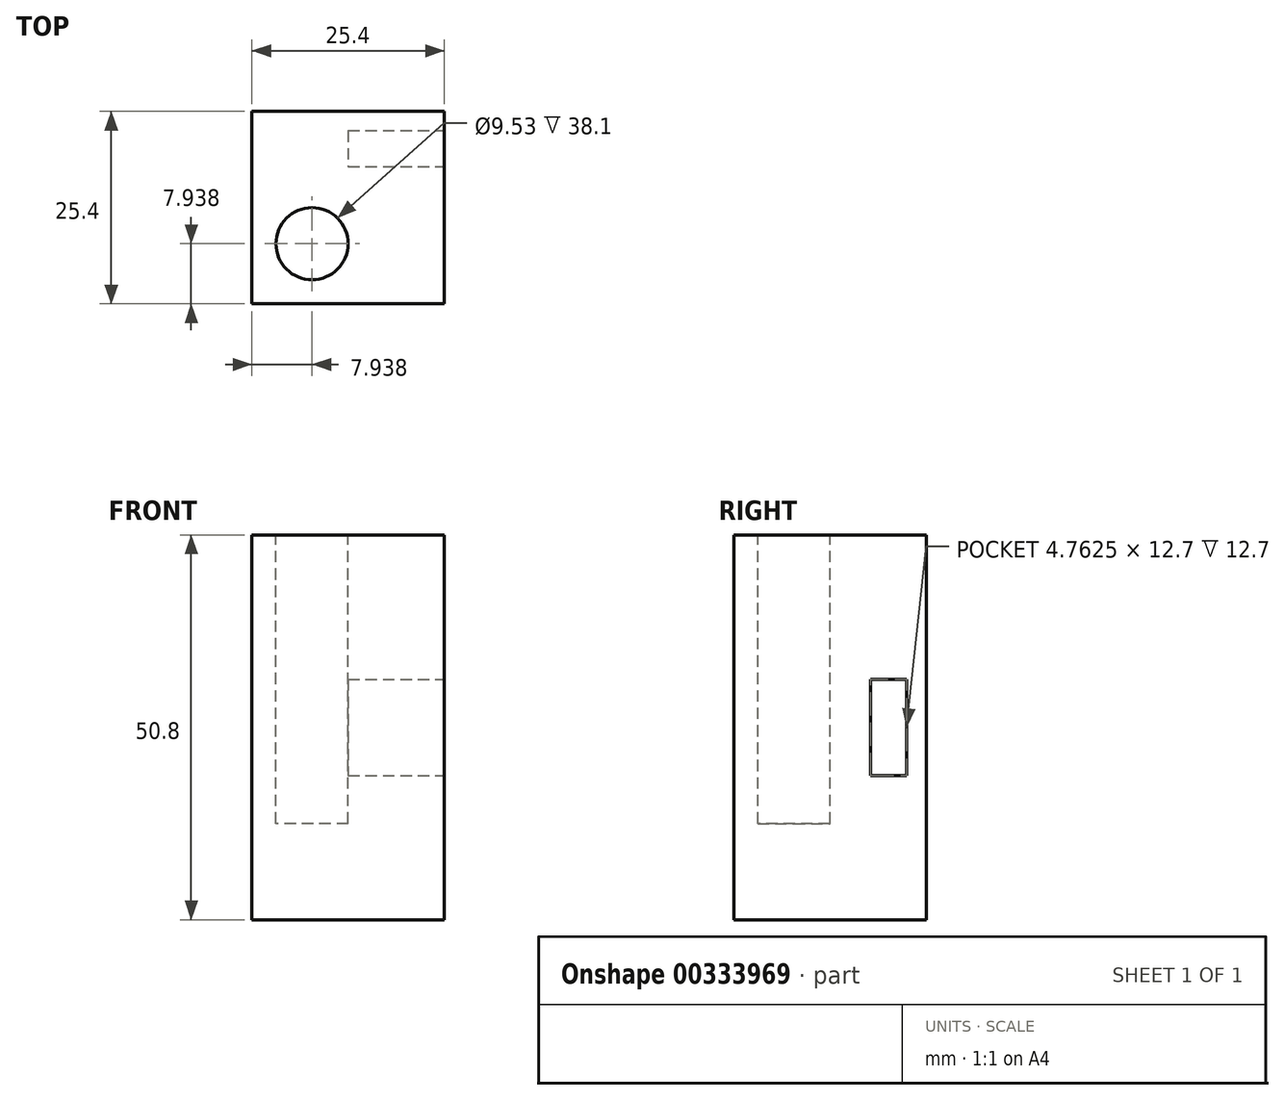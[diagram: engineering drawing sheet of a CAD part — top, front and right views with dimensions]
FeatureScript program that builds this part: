
annotation { "Feature Type Name" : "Feature", "Feature Type Description" : "" }
export const myFeature = defineFeature(function(context is Context, id is Id, definition is map)
    precondition{}
    {
        {
            var Q0;
            Q0=qCreatedBy(makeId("Top.planeOp"),FACE);
            var sketch = newSketch(context, id + "F0", { "sketchPlane" : qUnion([Q0])});
            skLineSegment(sketch, "E0.bottom", {"start": v(0, 0) * mm, "end": v(25.4, 0) * mm});
            skLineSegment(sketch, "E0.top", {"start": v(0, 25.4) * mm, "end": v(25.4, 25.4) * mm});
            skLineSegment(sketch, "E0.left", {"start": v(0, 0) * mm, "end": v(0, 25.4) * mm});
            skLineSegment(sketch, "E0.right", {"start": v(25.4, 0) * mm, "end": v(25.4, 25.4) * mm});
            skSolve(sketch);
        }
        {
            var Q0;
            Q0=makeQuery(id+"F0.imprint","IMPRINT",FACE,{"disambiguationData":[TD([[makeQuery(id+"F0.imprint","IMPRINT",EDGE,{"derivedFrom":sQuery(id+"F0.wireOp",EDGE,"E0.bottom")}),1.0]])]});
            extrude(context, id + "F1", {"entities" : qUnion([Q0]), "depth" : 50.8 * mm});
        }
        {
            var Q0;
            Q0=makeQuery(id+"F1.opExtrude","CAP_FACE",FACE,{"disambiguationData":[OSD([sQuery(id+"F0.wireOp",EDGE,"E0.bottom"),sQuery(id+"F0.wireOp",EDGE,"E0.top"),sQuery(id+"F0.wireOp",EDGE,"E0.left"),sQuery(id+"F0.wireOp",EDGE,"E0.right")])],"isStart":false});
            var sketch = newSketch(context, id + "F2", { "sketchPlane" : qUnion([Q0])});
            skCircle(sketch, "E1", {"center": v(7.94, 7.94) * mm, "radius": 4.76 * mm});
            skSolve(sketch);
        }
        {
            var Q0;
            Q0 = qSketchRegion(id + "F2", true);
            extrude(context, id + "F3", {"entities" : qUnion([Q0]), "operationType" : NewBodyOperationType.REMOVE, "oppositeDirection" : true, "depth" : 38.1 * mm});
        }
        {
            var Q0;
            Q0=makeQuery(id+"F1.opExtrude","SWEPT_FACE",FACE,{"disambiguationData":[OSD([sQuery(id+"F0.wireOp",EDGE,"E0.right")])]});
            var sketch = newSketch(context, id + "F4", { "sketchPlane" : qUnion([Q0])});
            skLineSegment(sketch, "E2.bottom", {"start": v(22.86, 31.75) * mm, "end": v(18.1, 31.75) * mm});
            skLineSegment(sketch, "E2.top", {"start": v(22.86, 19.05) * mm, "end": v(18.1, 19.05) * mm});
            skLineSegment(sketch, "E2.left", {"start": v(22.86, 31.75) * mm, "end": v(22.86, 19.05) * mm});
            skLineSegment(sketch, "E2.right", {"start": v(18.1, 31.75) * mm, "end": v(18.1, 19.05) * mm});
            skSolve(sketch);
        }
        {
            var Q0;
            Q0 = qSketchRegion(id + "F4", true);
            extrude(context, id + "F5", {"entities" : qUnion([Q0]), "operationType" : NewBodyOperationType.REMOVE, "oppositeDirection" : true, "depth" : 12.7 * mm});
        }
    });
